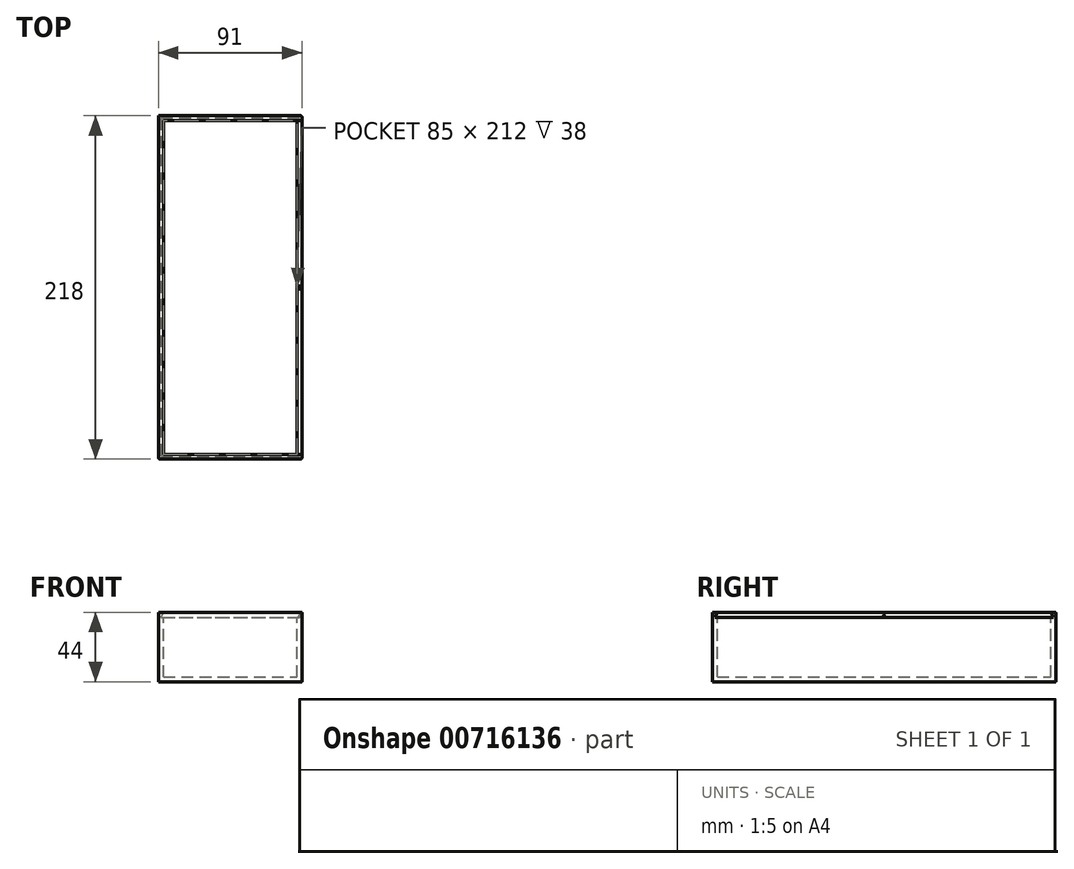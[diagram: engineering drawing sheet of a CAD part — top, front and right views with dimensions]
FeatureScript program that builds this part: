
annotation { "Feature Type Name" : "Feature", "Feature Type Description" : "" }
export const myFeature = defineFeature(function(context is Context, id is Id, definition is map)
    precondition{}
    {
        {
            assignVariable(context, id + "F0", {"name" : "WIDTH", "anyValue" : 91});
        }
        {
            assignVariable(context, id + "F1", {"name" : "LENGTH", "anyValue" : 218});
        }
        {
            assignVariable(context, id + "F2", {"name" : "BOXHEIGHT", "anyValue" : 41});
        }
        {
            assignVariable(context, id + "F3", {"name" : "THICKNESS", "anyValue" : 3});
        }
        {
            var Q0;
            Q0=qCreatedBy(makeId("Top.planeOp"),FACE);
            var sketch = newSketch(context, id + "F4", { "sketchPlane" : qUnion([Q0])});
            skLineSegment(sketch, "E0.bottom", {"start": v(0, 0) * mm, "end": v(91, 0) * mm});
            skLineSegment(sketch, "E0.top", {"start": v(0, 218) * mm, "end": v(91, 218) * mm});
            skLineSegment(sketch, "E0.left", {"start": v(0, 0) * mm, "end": v(0, 218) * mm});
            skLineSegment(sketch, "E0.right", {"start": v(91, 0) * mm, "end": v(91, 218) * mm});
            skLineSegment(sketch, "E1", {"start": v(-8.15, 109) * mm, "end": v(34.13, 109) * mm, "construction": true});
            skSolve(sketch);
        }
        {
            var Q0;
            Q0=qSketchRegion(id+"F4",true);
            extrude(context, id + "F5", {"entities" : qUnion([Q0]), "depth" : (getVariable(context, 'BOXHEIGHT')) * mm, "offsetDistance" : 25.4 * mm});
        }
        {
            var Q0;
            Q0=makeQuery(id+"F5.opExtrude","SWEPT_FACE",FACE,{"disambiguationData":[OSD([sQuery(id+"F4.wireOp",EDGE,"E0.right")])]});
            var sketch = newSketch(context, id + "F6", { "sketchPlane" : qUnion([Q0])});
            skLineSegment(sketch, "E2", {"start": v(0, 41) * mm, "end": v(0, 44) * mm});
            skLineSegment(sketch, "E3", {"start": v(0, 44) * mm, "end": v(3, 44) * mm});
            skLineSegment(sketch, "E4", {"start": v(3, 44) * mm, "end": v(1.5, 41) * mm});
            skLineSegment(sketch, "E5", {"start": v(1.5, 41) * mm, "end": v(0, 41) * mm});
            skLineSegment(sketch, "E6", {"start": v(218, 41) * mm, "end": v(218, 44) * mm});
            skLineSegment(sketch, "E7", {"start": v(218, 44) * mm, "end": v(215, 44) * mm});
            skLineSegment(sketch, "E8", {"start": v(215, 44) * mm, "end": v(216.5, 41) * mm});
            skLineSegment(sketch, "E9", {"start": v(216.5, 41) * mm, "end": v(218, 41) * mm});
            skSolve(sketch);
        }
        {
            var Q0;
            Q0=makeQuery(id+"F5.opExtrude","SWEPT_FACE",FACE,{"disambiguationData":[OSD([sQuery(id+"F4.wireOp",EDGE,"E0.bottom")])]});
            var sketch = newSketch(context, id + "F7", { "sketchPlane" : qUnion([Q0])});
            skLineSegment(sketch, "E10", {"start": v(0, 41) * mm, "end": v(0, 44) * mm});
            skLineSegment(sketch, "E11", {"start": v(0, 44) * mm, "end": v(3, 44) * mm});
            skLineSegment(sketch, "E12", {"start": v(3, 44) * mm, "end": v(1.5, 41) * mm});
            skLineSegment(sketch, "E13", {"start": v(1.5, 41) * mm, "end": v(0, 41) * mm});
            skSolve(sketch);
        }
        {
            var Q0;
            Q0 = qSketchRegion(id + "F7", true);
            extrude(context, id + "F8", {"entities" : qUnion([Q0]), "operationType" : NewBodyOperationType.ADD, "oppositeDirection" : true, "depth" : (getVariable(context, 'LENGTH')) * mm, "offsetDistance" : 25.4 * mm});
        }
        {
            var Q0;
            Q0 = qSketchRegion(id + "F6", true);
            extrude(context, id + "F9", {"entities" : qUnion([Q0]), "operationType" : NewBodyOperationType.ADD, "oppositeDirection" : true, "depth" : (getVariable(context, 'WIDTH')) * mm, "offsetDistance" : 25.4 * mm});
        }
        {
            var Q0;
            Q0=makeQuery(id+"F5.opExtrude","CAP_FACE",FACE,{"disambiguationData":[OSD([sQuery(id+"F4.wireOp",EDGE,"E0.bottom"),sQuery(id+"F4.wireOp",EDGE,"E0.top"),sQuery(id+"F4.wireOp",EDGE,"E0.left"),sQuery(id+"F4.wireOp",EDGE,"E0.right")])],"isStart":false});
            var sketch = newSketch(context, id + "F10", { "sketchPlane" : qUnion([Q0])});
            skLineSegment(sketch, "E14.bottom", {"start": v(3, 3) * mm, "end": v(88, 3) * mm});
            skLineSegment(sketch, "E14.top", {"start": v(3, 215) * mm, "end": v(88, 215) * mm});
            skLineSegment(sketch, "E14.left", {"start": v(3, 3) * mm, "end": v(3, 215) * mm});
            skLineSegment(sketch, "E14.right", {"start": v(88, 3) * mm, "end": v(88, 215) * mm});
            skSolve(sketch);
        }
        {
            var Q0;
            Q0 = qSketchRegion(id + "F10", true);
            extrude(context, id + "F11", {"entities" : qUnion([Q0]), "operationType" : NewBodyOperationType.REMOVE, "oppositeDirection" : true, "depth" : ((getVariable(context, 'BOXHEIGHT')) - getVariable(context, 'THICKNESS')) * mm, "offsetDistance" : 25.4 * mm});
        }
        {
            var Q0;
            Q0=makeQuery(id+"F9.boolean.opBoolean","MERGE",EDGE,{"derivedFrom":[makeQuery(id+"F5.opExtrude","SWEPT_EDGE",EDGE,{"disambiguationData":[OSD([sQuery(id+"F4.wireOp",EDGE,"E0.bottom"),sQuery(id+"F4.wireOp",EDGE,"E0.right")])]}),makeQuery(id+"F9.opExtrude","CAP_EDGE",EDGE,{"disambiguationData":[OSD([sQuery(id+"F6.wireOp",EDGE,"E2")])],"isStart":true})]});
            var Q1;
            Q1=makeQuery(id+"F9.boolean.opBoolean","MERGE",EDGE,{"derivedFrom":[makeQuery(id+"F5.opExtrude","SWEPT_EDGE",EDGE,{"disambiguationData":[OSD([sQuery(id+"F4.wireOp",EDGE,"E0.top"),sQuery(id+"F4.wireOp",EDGE,"E0.right")])]}),makeQuery(id+"F9.opExtrude","CAP_EDGE",EDGE,{"disambiguationData":[OSD([sQuery(id+"F6.wireOp",EDGE,"E6")])],"isStart":true})]});
            var Q2;
            Q2=makeQuery(id+"F8.boolean.opBoolean","MERGE",EDGE,{"derivedFrom":[makeQuery(id+"F5.opExtrude","SWEPT_EDGE",EDGE,{"disambiguationData":[OSD([sQuery(id+"F4.wireOp",EDGE,"E0.bottom"),sQuery(id+"F4.wireOp",EDGE,"E0.left")])]}),makeQuery(id+"F8.opExtrude","CAP_EDGE",EDGE,{"disambiguationData":[OSD([sQuery(id+"F7.wireOp",EDGE,"E10")])],"isStart":true})]});
            fillet(context, id + "F12", {"entities" : qUnion([Q0, Q1, Q2]), "radius" : getVariable(context, 'THICKNESS') / 4 * mm, "tangentPropagation" : true, "allowEdgeOverflow" : false});
        }
        {
            var Q0;
            Q0=makeQuery(id+"F5.opExtrude","CAP_FACE",FACE,{"disambiguationData":[OSD([sQuery(id+"F4.wireOp",EDGE,"E0.bottom"),sQuery(id+"F4.wireOp",EDGE,"E0.top"),sQuery(id+"F4.wireOp",EDGE,"E0.left"),sQuery(id+"F4.wireOp",EDGE,"E0.right")])],"isStart":false});
            var sketch = newSketch(context, id + "F13", { "sketchPlane" : qUnion([Q0])});
            skLineSegment(sketch, "E15", {"start": v(26.48, 109) * mm, "end": v(21.57, 109) * mm, "construction": true});
            skArc(sketch, "E16", {"start": v(90.5, 109) * mm, "mid": v(89.5, 110) * mm, "end": v(88.5, 109) * mm});
            skLineSegment(sketch, "E17", {"start": v(90.5, 109) * mm, "end": v(88.5, 109) * mm});
            skSolve(sketch);
        }
        {
            var Q0;
            Q0=makeQuery(id+"F13.imprint","IMPRINT",FACE,{"disambiguationData":[TD([[makeQuery(id+"F13.imprint","IMPRINT",EDGE,{"derivedFrom":sQuery(id+"F13.wireOp",EDGE,"E16")}),1.0]])]});
            var Q1;
            Q1=sQuery(id+"F13.wireOp",EDGE,"E16");
            var Q2;
            Q2=sQuery(id+"F13.wireOp",EDGE,"E15");
            revolve(context, id + "F14", {"operationType" : NewBodyOperationType.ADD, "surfaceOperationType" : NewSurfaceOperationType.NEW, "entities" : qUnion([Q0]), "surfaceEntities" : qUnion([Q1]), "axis" : qUnion([Q2]), "revolveType" : RevolveType.FULL});
        }
    });
